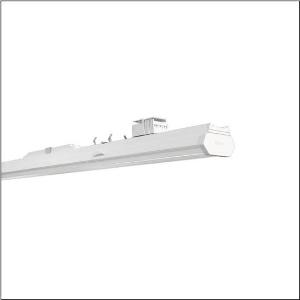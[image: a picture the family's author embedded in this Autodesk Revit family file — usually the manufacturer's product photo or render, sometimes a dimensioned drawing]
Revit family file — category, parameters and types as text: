
# Revit family: licross_r__21_protected_ho_52td1bmn4exm_7a17
name_source: partatom
category: Lighting Fixtures
units: mm (PartAtom-declared; Revit-internal decimal feet)

## family parameters
Cut with Voids When Loaded = No
Host = Face
Light Source = No
Part Type = Normal
Room Calculation Point = No
Round Connector Dimension = Use Diameter
Shared = No

## types (1)
- --- (1 x LED, 14040 lm, 83.2 W, 4000K)
    Apparent Load = 83 VA
    CIE Flux Codes = 54 82 95 97 100
    Color Rendering = 80
    Color Temperature = 4000K
    Default Elevation = 1800 mm
    Description = Licross® 21 Protected HO, luminaire insert, of sheet steel, galvanised, coil coated, white, length: 1.500mm, width: 90mm, height: 103mm, LED rated luminous flux: 14.040lm, light colour: 840, control gear: ON/OFF Multilumen, with plug, 3-pole, with phase selection, mains connection: 220..240V, AC, 50/60Hz, rated input power: 83W, halogen-free wiring, primary optical cover: cover, of PMMA, light emission: direct distribution, primary light characteristic: symmetric, protection rating (complete): IP54, insulation class (complete): insulation class I (protective earthing), certification: CE, ENEC, VDE, UKCA, protection symbol: D if used in an environment with non-conductive dust loads with corresponding accessories, impact resistance: IK06, permissible ambient temperature for indoor applications: -35..+35°C, corresponds to IFS (International Featured Standards) requirements for safety and quality in the food industry, reducing of maximum allowable ambient temperature of 5°C with ceiling mounting, LABS conformity tested according to VDMA 24364:2018-05, packaging unit: 1 piece
    Height = 92 mm
    Lamp = 1 x LED
    Lamp Light Flux = 14040 lm
    Lamp Power = 83.2 W
    Lamp count = 1
    Length = 1500 mm
    Luminous efficacy = 169 lm/W
    Manufacturer = Siteco
    ModVariant = No
    Model = 52TD1BMN4EXM
    Mounting Place = Ceiling
    Mounting Type = Pendant
    Number of Poles = 1
    OnlyDefault = Yes
    Power Factor = 1
    Product Name = Licross® 21 Protected HO
    Product group = luminaire insert
    ProductGroupID = 901
    Protection Class = Protection class I
    Protection Degree = IP 54
    RLX_Detail_Level = 1
    RLX_Emergency_Light_Flux = 0 lm
    RLX_Emergency_Type = 0
    RLX_Emergency_Type_DB = No
    RlxData = <blob elided: 22061 chars, md5=2e794248>
    Socket = socket
    Standby Power = 0 W
    System Light Flux = 14040 lm
    System Power = 83 W
    Type Comments = factory setting: luminous flux: 100 % | (A | C | E) | 195 mA
    Type Image = l_1256148.jpg
    URL = http://relux.com
    VarID = @adj_078055
    Voltage = 0 V
    Weight = 0.00 kg
    Width = 88 mm

## geometry (parser evidence)
native form markers: Blend x4, Sweep x10
no freeform markers — native parametric forms only
